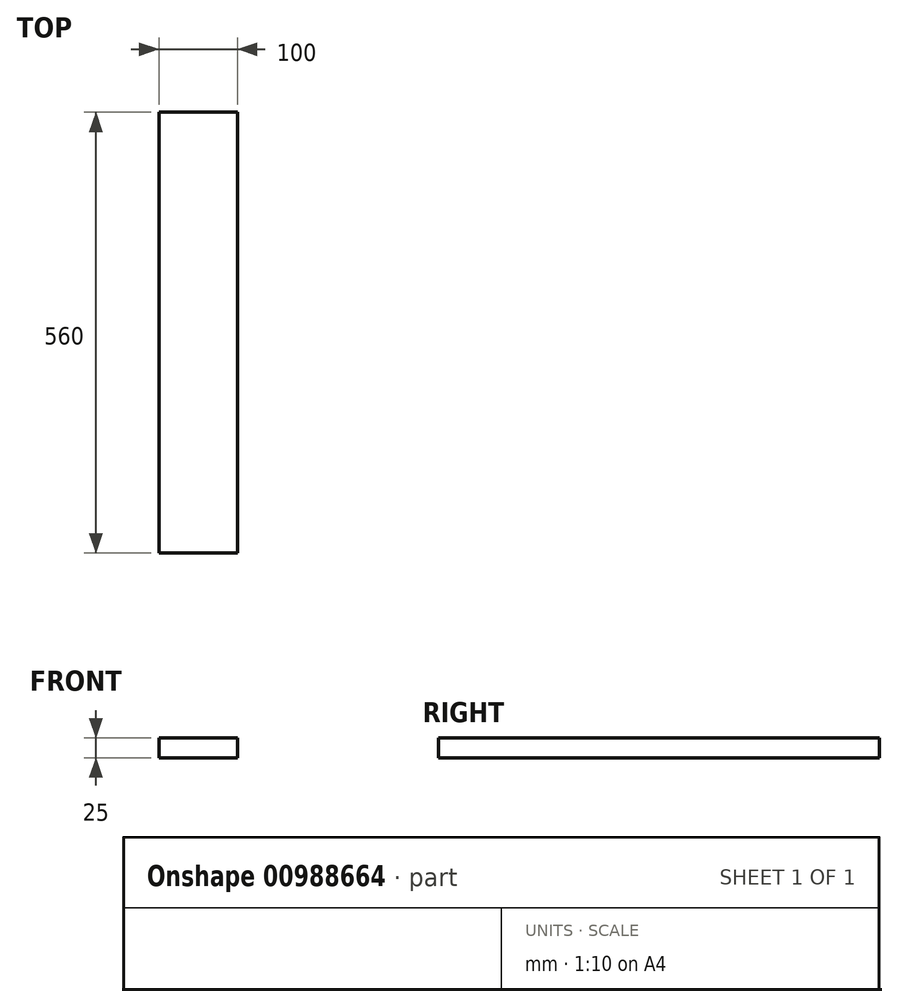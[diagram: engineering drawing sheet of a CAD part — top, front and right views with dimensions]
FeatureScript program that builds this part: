
annotation { "Feature Type Name" : "Feature", "Feature Type Description" : "" }
export const myFeature = defineFeature(function(context is Context, id is Id, definition is map)
    precondition{}
    {
        {
            var Q0;
            Q0=qCreatedBy(makeId("Top.planeOp"),FACE);
            var sketch = newSketch(context, id + "F0", { "sketchPlane" : qUnion([Q0])});
            skLineSegment(sketch, "E0.bottom", {"start": v(0, 0) * mm, "end": v(-100, 0) * mm});
            skLineSegment(sketch, "E0.top", {"start": v(0, 560) * mm, "end": v(-100, 560) * mm});
            skLineSegment(sketch, "E0.left", {"start": v(0, 0) * mm, "end": v(0, 560) * mm});
            skLineSegment(sketch, "E0.right", {"start": v(-100, 0) * mm, "end": v(-100, 560) * mm});
            skSolve(sketch);
        }
        {
            var Q0;
            Q0 = qSketchRegion(id + "F0", true);
            extrude(context, id + "F1", {"entities" : qUnion([Q0]), "depth" : 25 * mm, "offsetDistance" : 25 * mm});
        }
        {
            var Q0;
            Q0 = qSketchRegion(id + "F0", true);
            extrude(context, id + "F2", {"entities" : qUnion([Q0]), "operationType" : NewBodyOperationType.ADD, "depth" : 25 * mm, "offsetDistance" : 25 * mm});
        }
        {
            var Q0;
            Q0 = qSketchRegion(id + "F0", true);
            extrude(context, id + "F3", {"entities" : qUnion([Q0]), "operationType" : NewBodyOperationType.ADD, "depth" : 25 * mm, "offsetDistance" : 25 * mm});
        }
        {
            var Q0;
            Q0 = qSketchRegion(id + "F0", true);
            extrude(context, id + "F4", {"entities" : qUnion([Q0]), "operationType" : NewBodyOperationType.ADD, "depth" : 25 * mm, "offsetDistance" : 25 * mm});
        }
    });
